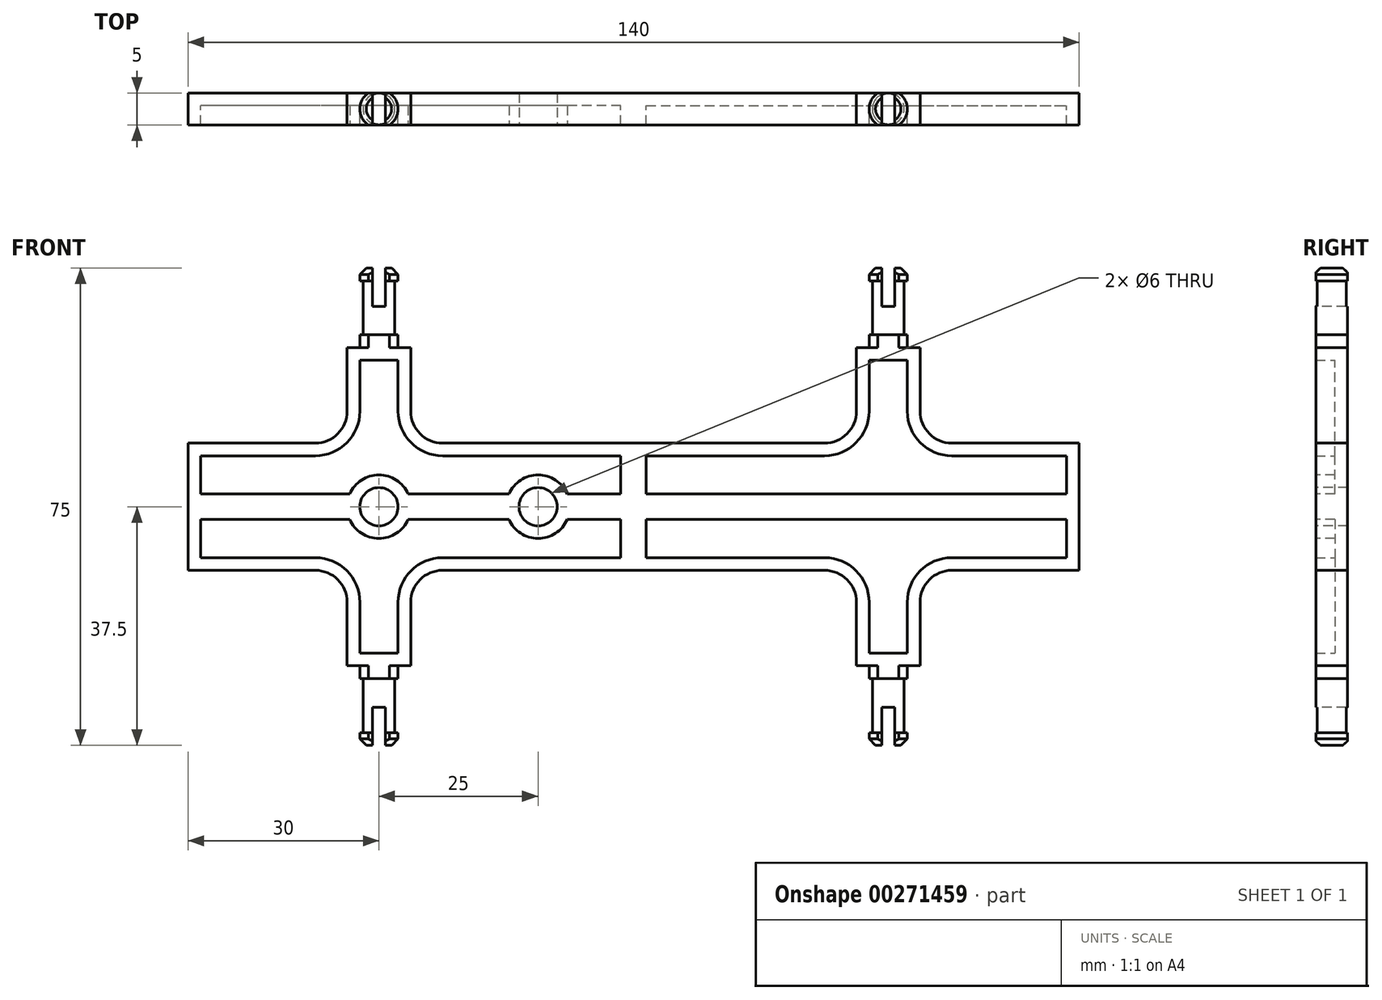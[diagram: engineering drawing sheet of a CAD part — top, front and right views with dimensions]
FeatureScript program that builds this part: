
annotation { "Feature Type Name" : "Feature", "Feature Type Description" : "" }
export const myFeature = defineFeature(function(context is Context, id is Id, definition is map)
    precondition{}
    {
        {
            var Q0;
            Q0=qCreatedBy(makeId("Front.planeOp"),FACE);
            var sketch = newSketch(context, id + "F0", { "sketchPlane" : qUnion([Q0])});
            skLineSegment(sketch, "E0.bottom", {"start": v(0, 0) * mm, "end": v(70, 0) * mm});
            skLineSegment(sketch, "E0.top", {"start": v(0, 10) * mm, "end": v(30, 10) * mm});
            skLineSegment(sketch, "E0.left", {"start": v(0, 0) * mm, "end": v(0, 10) * mm});
            skLineSegment(sketch, "E0.right", {"start": v(70, 0) * mm, "end": v(70, 10) * mm});
            skLineSegment(sketch, "E1.top", {"start": v(35, 25) * mm, "end": v(45, 25) * mm});
            skLineSegment(sketch, "E1.left", {"start": v(35, 15) * mm, "end": v(35, 25) * mm});
            skLineSegment(sketch, "E1.right", {"start": v(45, 15) * mm, "end": v(45, 25) * mm});
            skLineSegment(sketch, "E2.trimOffspring", {"start": v(50, 10) * mm, "end": v(70, 10) * mm});
            skPoint(sketch, "E3.visualSharp", {"position": v(35, 10) * mm});
            skArc(sketch, "E3.filletArc", {"start": v(30, 10) * mm, "mid": v(33.54, 11.46) * mm, "end": v(35, 15) * mm});
            skPoint(sketch, "E4.visualSharp", {"position": v(45, 10) * mm});
            skArc(sketch, "E4.filletArc", {"start": v(45, 15) * mm, "mid": v(46.46, 11.46) * mm, "end": v(50, 10) * mm});
            skSolve(sketch);
        }
        {
            var Q0;
            Q0 = qSketchRegion(id + "F0", true);
            extrude(context, id + "F1", {"entities" : qUnion([Q0]), "depth" : 5 * mm, "symmetric" : true});
        }
        {
            var Q0;
            Q0=makeQuery(id+"F1.opExtrude","CAP_FACE",FACE,{"disambiguationData":[OSD([sQuery(id+"F0.wireOp",EDGE,"E0.bottom"),sQuery(id+"F0.wireOp",EDGE,"E0.top"),sQuery(id+"F0.wireOp",EDGE,"E0.left"),sQuery(id+"F0.wireOp",EDGE,"E0.right"),sQuery(id+"F0.wireOp",EDGE,"E1.top"),sQuery(id+"F0.wireOp",EDGE,"E1.left"),sQuery(id+"F0.wireOp",EDGE,"E1.right"),sQuery(id+"F0.wireOp",EDGE,"E2.trimOffspring"),sQuery(id+"F0.wireOp",EDGE,"E3.filletArc"),sQuery(id+"F0.wireOp",EDGE,"E4.filletArc")])],"isStart":false});
            shell(context, id + "F2", {"entities" : qUnion([Q0]), "thickness" : 2 * mm});
        }
        {
            var Q0;
            Q0=qCreatedBy(makeId("Front.planeOp"),FACE);
            var sketch = newSketch(context, id + "F3", { "sketchPlane" : qUnion([Q0])});
            skLineSegment(sketch, "E5", {"start": v(37, 25) * mm, "end": v(37, 27) * mm});
            skLineSegment(sketch, "E6", {"start": v(37, 27) * mm, "end": v(37.5, 27) * mm});
            skLineSegment(sketch, "E7", {"start": v(37.5, 27) * mm, "end": v(37.5, 35.5) * mm});
            skLineSegment(sketch, "E8", {"start": v(37.5, 35.5) * mm, "end": v(37, 35.5) * mm});
            skLineSegment(sketch, "E9", {"start": v(37, 35.5) * mm, "end": v(37, 37.5) * mm});
            skLineSegment(sketch, "E10", {"start": v(37, 37.5) * mm, "end": v(40, 37.5) * mm});
            skLineSegment(sketch, "E11", {"start": v(40, 37.5) * mm, "end": v(40, 25) * mm});
            skLineSegment(sketch, "E12", {"start": v(40, 25) * mm, "end": v(37, 25) * mm});
            skSolve(sketch);
        }
        {
            var Q0;
            Q0 = qSketchRegion(id + "F3", true);
            var Q1;
            Q1=sQuery(id+"F3.wireOp",EDGE,"E11");
            revolve(context, id + "F4", {"operationType" : NewBodyOperationType.ADD, "entities" : qUnion([Q0]), "axis" : qUnion([Q1]), "revolveType" : RevolveType.FULL});
        }
        {
            var Q0;
            Q0=makeQuery(id+"F4.opRevolve","SWEPT_FACE",FACE,{"disambiguationData":[OSD([sQuery(id+"F3.wireOp",EDGE,"E10")])]});
            chamfer(context, id + "F5", {"entities" : qUnion([Q0]), "width" : 1 * mm, "tangentPropagation" : true});
        }
        {
            var Q0;
            Q0=makeQuery(id+"F4.opRevolve","SWEPT_FACE",FACE,{"disambiguationData":[OSD([sQuery(id+"F3.wireOp",EDGE,"E10")])]});
            var sketch = newSketch(context, id + "F6", { "sketchPlane" : qUnion([Q0])});
            skLineSegment(sketch, "E13.bottom", {"start": v(-2.52, 2.5) * mm, "end": v(73.11, 2.5) * mm});
            skLineSegment(sketch, "E13.top", {"start": v(-2.52, -2.5) * mm, "end": v(73.11, -2.5) * mm});
            skLineSegment(sketch, "E13.left", {"start": v(-2.52, 2.5) * mm, "end": v(-2.52, -2.5) * mm});
            skLineSegment(sketch, "E13.right", {"start": v(73.11, 2.5) * mm, "end": v(73.11, -2.5) * mm});
            skSolve(sketch);
        }
        {
            var Q0;
            Q0 = qSketchRegion(id + "F6", true);
            extrude(context, id + "F7", {"entities" : qUnion([Q0]), "operationType" : NewBodyOperationType.INTERSECT, "endBound" : BoundingType.THROUGH_ALL, "oppositeDirection" : true, "depth" : 25 * mm});
        }
        {
            var Q0;
            Q0=makeQuery(id+"F4.opRevolve","SWEPT_FACE",FACE,{"disambiguationData":[OSD([sQuery(id+"F3.wireOp",EDGE,"E10")])]});
            var sketch = newSketch(context, id + "F8", { "sketchPlane" : qUnion([Q0])});
            skLineSegment(sketch, "E14.bottom", {"start": v(39, 4.5) * mm, "end": v(41, 4.5) * mm});
            skLineSegment(sketch, "E14.top", {"start": v(39, -5.53) * mm, "end": v(41, -5.53) * mm});
            skLineSegment(sketch, "E14.left", {"start": v(39, 4.5) * mm, "end": v(39, -5.53) * mm});
            skLineSegment(sketch, "E14.right", {"start": v(41, 4.5) * mm, "end": v(41, -5.53) * mm});
            skSolve(sketch);
        }
        {
            var Q0;
            Q0 = qSketchRegion(id + "F8", true);
            extrude(context, id + "F9", {"entities" : qUnion([Q0]), "operationType" : NewBodyOperationType.REMOVE, "oppositeDirection" : true, "depth" : 6 * mm});
        }
        {
            var Q0;
            Q0=makeQuery(id+"F1.opExtrude","SWEPT_BODY",BODY,{"disambiguationData":[OSD([sQuery(id+"F0.wireOp",EDGE,"E0.bottom"),sQuery(id+"F0.wireOp",EDGE,"E0.top"),sQuery(id+"F0.wireOp",EDGE,"E0.left"),sQuery(id+"F0.wireOp",EDGE,"E0.right"),sQuery(id+"F0.wireOp",EDGE,"E1.top"),sQuery(id+"F0.wireOp",EDGE,"E1.left"),sQuery(id+"F0.wireOp",EDGE,"E1.right"),sQuery(id+"F0.wireOp",EDGE,"E2.trimOffspring"),sQuery(id+"F0.wireOp",EDGE,"E3.filletArc"),sQuery(id+"F0.wireOp",EDGE,"E4.filletArc")])]});
            var Q1;
            Q1=qCreatedBy(makeId("Top.planeOp"),FACE);
            mirror(context, id + "F10", {"operationType" : NewBodyOperationType.ADD, "entities" : qUnion([Q0]), "mirrorPlane" : qUnion([Q1])});
        }
        {
            var Q0;
            Q0=makeQuery(id+"F1.opExtrude","SWEPT_BODY",BODY,{"disambiguationData":[OSD([sQuery(id+"F0.wireOp",EDGE,"E0.bottom"),sQuery(id+"F0.wireOp",EDGE,"E0.top"),sQuery(id+"F0.wireOp",EDGE,"E0.left"),sQuery(id+"F0.wireOp",EDGE,"E0.right"),sQuery(id+"F0.wireOp",EDGE,"E1.top"),sQuery(id+"F0.wireOp",EDGE,"E1.left"),sQuery(id+"F0.wireOp",EDGE,"E1.right"),sQuery(id+"F0.wireOp",EDGE,"E2.trimOffspring"),sQuery(id+"F0.wireOp",EDGE,"E3.filletArc"),sQuery(id+"F0.wireOp",EDGE,"E4.filletArc")])]});
            var Q1;
            Q1=qCreatedBy(makeId("Right.planeOp"),FACE);
            mirror(context, id + "F11", {"operationType" : NewBodyOperationType.ADD, "entities" : qUnion([Q0]), "mirrorPlane" : qUnion([Q1])});
        }
        {
            var Q0;
            {var subQ0=makeQuery(id+"F7.boolean.opBoolean","MERGE",FACE,{"derivedFrom":[makeQuery(id+"F1.opExtrude","CAP_FACE",FACE,{"disambiguationData":[OSD([sQuery(id+"F0.wireOp",EDGE,"E0.bottom"),sQuery(id+"F0.wireOp",EDGE,"E0.top"),sQuery(id+"F0.wireOp",EDGE,"E0.left"),sQuery(id+"F0.wireOp",EDGE,"E0.right"),sQuery(id+"F0.wireOp",EDGE,"E1.top"),sQuery(id+"F0.wireOp",EDGE,"E1.left"),sQuery(id+"F0.wireOp",EDGE,"E1.right"),sQuery(id+"F0.wireOp",EDGE,"E2.trimOffspring"),sQuery(id+"F0.wireOp",EDGE,"E3.filletArc"),sQuery(id+"F0.wireOp",EDGE,"E4.filletArc")])],"isStart":false}),makeQuery(id+"F7.boolean.toolComplement.opBoolean","COPY",FACE,{"derivedFrom":makeQuery(id+"F7.opExtrude","SWEPT_FACE",FACE,{"disambiguationData":[OSD([sQuery(id+"F6.wireOp",EDGE,"E13.top")])]})})]});var subQ1=makeQuery(id+"F10.boolean.opBoolean","MERGE",FACE,{"derivedFrom":[subQ0,makeQuery(id+"F10.opPattern","COPY",FACE,{"derivedFrom":subQ0,"instanceName":"1"})]});Q0=makeQuery(id+"F11.boolean.opBoolean","MERGE",FACE,{"derivedFrom":[subQ1,makeQuery(id+"F11.opPattern","COPY",FACE,{"derivedFrom":subQ1,"instanceName":"1"})]});}
            var sketch = newSketch(context, id + "F12", { "sketchPlane" : qUnion([Q0])});
            skCircle(sketch, "E15", {"center": v(-40, 0) * mm, "radius": 5 * mm});
            skCircle(sketch, "E16", {"center": v(-15, 0) * mm, "radius": 5 * mm});
            skSolve(sketch);
        }
        {
            var Q0;
            Q0 = qSketchRegion(id + "F12", true);
            extrude(context, id + "F13", {"entities" : qUnion([Q0]), "operationType" : NewBodyOperationType.ADD, "endBound" : BoundingType.UP_TO_NEXT, "oppositeDirection" : true, "depth" : 25 * mm});
        }
        {
            var Q0;
            {var subQ0=makeQuery(id+"F7.boolean.opBoolean","MERGE",FACE,{"derivedFrom":[makeQuery(id+"F1.opExtrude","CAP_FACE",FACE,{"disambiguationData":[OSD([sQuery(id+"F0.wireOp",EDGE,"E0.bottom"),sQuery(id+"F0.wireOp",EDGE,"E0.top"),sQuery(id+"F0.wireOp",EDGE,"E0.left"),sQuery(id+"F0.wireOp",EDGE,"E0.right"),sQuery(id+"F0.wireOp",EDGE,"E1.top"),sQuery(id+"F0.wireOp",EDGE,"E1.left"),sQuery(id+"F0.wireOp",EDGE,"E1.right"),sQuery(id+"F0.wireOp",EDGE,"E2.trimOffspring"),sQuery(id+"F0.wireOp",EDGE,"E3.filletArc"),sQuery(id+"F0.wireOp",EDGE,"E4.filletArc")])],"isStart":false}),makeQuery(id+"F7.boolean.toolComplement.opBoolean","COPY",FACE,{"derivedFrom":makeQuery(id+"F7.opExtrude","SWEPT_FACE",FACE,{"disambiguationData":[OSD([sQuery(id+"F6.wireOp",EDGE,"E13.top")])]})})]});var subQ1=makeQuery(id+"F10.boolean.opBoolean","MERGE",FACE,{"derivedFrom":[subQ0,makeQuery(id+"F10.opPattern","COPY",FACE,{"derivedFrom":subQ0,"instanceName":"1"})]});Q0=makeQuery(id+"F13.boolean.opBoolean","MERGE",FACE,{"derivedFrom":[makeQuery(id+"F11.boolean.opBoolean","MERGE",FACE,{"derivedFrom":[subQ1,makeQuery(id+"F11.opPattern","COPY",FACE,{"derivedFrom":subQ1,"instanceName":"1"})]}),makeQuery(id+"F13.opExtrude","CAP_FACE",FACE,{"disambiguationData":[OSD([sQuery(id+"F12.wireOp",EDGE,"E15")])],"isStart":true}),makeQuery(id+"F13.opExtrude","CAP_FACE",FACE,{"disambiguationData":[OSD([sQuery(id+"F12.wireOp",EDGE,"E16")])],"isStart":true})]});}
            var sketch = newSketch(context, id + "F14", { "sketchPlane" : qUnion([Q0])});
            skPoint(sketch, "E17", {"position": v(-40, 0) * mm});
            skPoint(sketch, "E18", {"position": v(-15, 0) * mm});
            skSolve(sketch);
        }
        {
            var Q0;
            Q0=sQuery(id+"F14.wireOp",VERTEX,"E17");
            var Q1;
            Q1=sQuery(id+"F14.wireOp",VERTEX,"E18");
            var Q2;
            Q2=makeQuery(id+"F1.opExtrude","SWEPT_BODY",BODY,{"disambiguationData":[OSD([sQuery(id+"F0.wireOp",EDGE,"E0.bottom"),sQuery(id+"F0.wireOp",EDGE,"E0.top"),sQuery(id+"F0.wireOp",EDGE,"E0.left"),sQuery(id+"F0.wireOp",EDGE,"E0.right"),sQuery(id+"F0.wireOp",EDGE,"E1.top"),sQuery(id+"F0.wireOp",EDGE,"E1.left"),sQuery(id+"F0.wireOp",EDGE,"E1.right"),sQuery(id+"F0.wireOp",EDGE,"E2.trimOffspring"),sQuery(id+"F0.wireOp",EDGE,"E3.filletArc"),sQuery(id+"F0.wireOp",EDGE,"E4.filletArc")])]});
            hole(context, id + "F15", {"style" : HoleStyle.SIMPLE, "endStyle" : HoleEndStyle.THROUGH, "holeDiameter" : 6 * mm, "tappedDepth" : 12 * mm, "tapClearance" : 3, "locations" : qUnion([Q0, Q1]), "scope" : qUnion([Q2])});
        }
    });
